# Revit family: QF_COMCATER ALL BRANDS_S86
name_source: partatom
category: Specialty Equipment
revit_build: Autodesk Revit 2014 (Build: 20140709_2115(x64)
units: mm (PartAtom-declared; Revit-internal decimal feet)

## types (2) — shared parameters
Accessory = No
Assembly Code = E1090320
Depth Actual = 515 mm
Description = GAS SALAMANDER
Gas Flow = 0.0 L/s
Gas Size = 19 mm
Gas Size Flexible = 0 mm
Height Actual = 440 mm  [stored 1.44357 ft]
Length Actual = 860 mm  [stored 2.82152 ft]
Manufacturer = TRUEHEAT
Model = S86
Type Comments = The Australian owned and designed* Trueheat RC Series of Gas Cooking Equipment has been developed for the restaurant and cafe market with a high quality finish, designed to fulfill the busy demands within a commercial kitchen.
The S86 is a gas heated, heavy duty salamander with fully adjustable height cooking shelf. Two powerful 14MJ high speed gas burners radiate intense heat, which seals in the natural flavours to leave a grilled appearance on steaks, chicken, seafood and vegetable.

## per-type parameters (varying)
| type | BTUH | Gas power kW | Nominal Gas power |
| S86_Natural Gas | 6700 W | 6.7 | 6700 W |
| S86_LPG | 6200 W | 6.2 | 6200 W |

note: [stored X ft] marks values corroborated as IEEE doubles in the binary element streams (Revit-internal decimal feet)

## geometry (parser evidence)
native form markers: Sweep x3
no freeform markers — native parametric forms only
